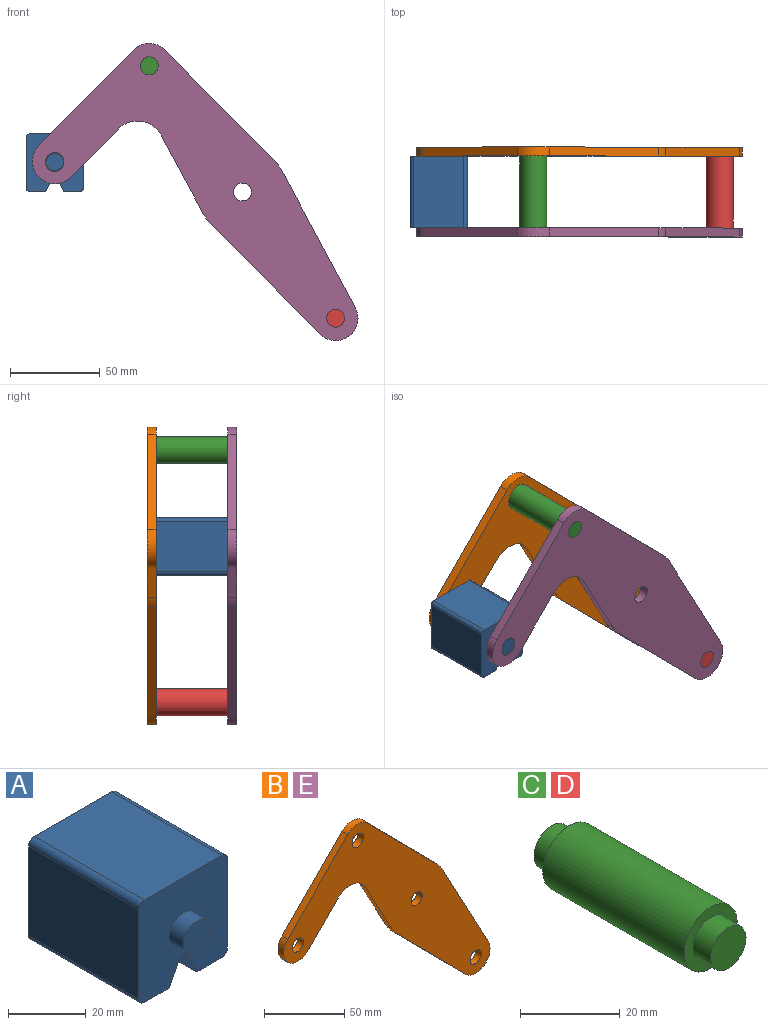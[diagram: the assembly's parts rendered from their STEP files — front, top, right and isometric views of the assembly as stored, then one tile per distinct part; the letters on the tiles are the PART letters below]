
ASSEMBLY  parts=5 mates=3
PART A: 18 faces, bbox 32.1x50x32.1 mm
  f0: plane 40x28.08mm, normal (1,0,0), area 1123.1mm2, adj f4,f10,f13,f14
  f1: plane 40x9.04mm, normal (0,0,-1), area 361.6mm2, adj f2,f4,f10,f14
  f2: plane 40x6.42mm, normal (-0.89,0,-0.45), area 287.2mm2, adj f1,f4,f10,f15
  f3: plane 40x6.42mm, normal (0.89,0,-0.45), area 287.2mm2, adj f4,f5,f10,f15
  f4: plane 32.08x32.08mm, normal (0,-1,0), area 900.6mm2, adj f0,f1,f2,f3,f5,f6,f7,f9
  f5: plane 40x9.04mm, normal (0,0,-1), area 361.6mm2, adj f3,f4,f10,f16
  f6: plane 40x28.08mm, normal (0,0,1), area 1123.1mm2, adj f4,f10,f13,f17
  f7: plane 40x28.08mm, normal (-1,0,0), area 1123.1mm2, adj f4,f10,f16,f17
  f8: plane 10x10mm, normal (0,-1,0), area 78.5mm2, adj f9
  f9: cylinder r=5mm len=10mm, axis (0,1,0), area 157.1mm2, adj f4,f8
  f10: plane 32.08x32.08mm, normal (0,1,0), area 900.6mm2, adj f0,f1,f2,f3,f5,f6,f7,f12
  f11: plane 10x10mm, normal (0,1,0), area 78.5mm2, adj f12
  f12: cylinder r=5mm len=10mm, axis (0,-1,0), area 157.1mm2, adj f10,f11
  f13: cylinder r=2mm len=40mm, axis (0,1,0), area 125.7mm2, adj f0,f4,f6,f10
  f14: cylinder r=2mm len=40mm, axis (0,-1,0), area 125.7mm2, adj f0,f1,f4,f10
  f15: cylinder r=2mm len=40mm, axis (0,1,0), area 177.1mm2, adj f2,f3,f4,f10
  f16: cylinder r=2mm len=40mm, axis (0,1,0), area 125.7mm2, adj f4,f5,f7,f10
  f17: cylinder r=2mm len=40mm, axis (0,-1,0), area 125.7mm2, adj f4,f6,f7,f10
PART B: 18 faces, bbox 181.7x5x165.8 mm
  f0: plane 43.49x23.35mm, normal (-0.88,0,-0.47), area 246.8mm2, adj f1,f14,f16,f17
  f1: cylinder r=25mm len=5.75mm, axis (0,1,0), area 35.8mm2, adj f0,f2,f16,f17
  f2: plane 61.6x60.87mm, normal (-0.71,0,-0.7), area 433mm2, adj f1,f3,f16,f17
  f3: cylinder r=12.5mm len=21.39mm, axis (0,1,0), area 178.4mm2, adj f2,f4,f16,f17
  f4: plane 76.3x40.96mm, normal (0.88,0,0.47), area 433mm2, adj f3,f5,f16,f17
  f5: cylinder r=25mm len=5.75mm, axis (0,1,0), area 35.8mm2, adj f4,f6,f16,f17
  f6: plane 61.6x60.87mm, normal (0.71,0,0.7), area 433mm2, adj f5,f7,f16,f17
  f7: cylinder r=12.5mm len=17.78mm, axis (0,1,0), area 98.9mm2, adj f6,f8,f16,f17
  f8: plane 53.35x52.71mm, normal (-0.71,0,0.7), area 375mm2, adj f7,f9,f16,f17
  f9: cylinder r=12.5mm len=21.39mm, axis (0,1,0), area 196.3mm2, adj f8,f10,f16,f17
  f10: plane 26.86x26.54mm, normal (0.71,0,-0.7), area 188.8mm2, adj f9,f14,f16,f17
  f11: cylinder r=5mm len=10mm, axis (0,1,0), area 157.1mm2, adj f16,f17
  f12: cylinder r=5mm len=10mm, axis (0,1,0), area 157.1mm2, adj f16,f17
  f13: cylinder r=5mm len=10mm, axis (0,1,0), area 157.1mm2, adj f16,f17
  f14: cylinder r=15mm len=23.89mm, axis (0,1,0), area 140.2mm2, adj f0,f10,f16,f17
  f15: cylinder r=5mm len=10mm, axis (0,1,0), area 157.1mm2, adj f16,f17
  f16: plane 181.66x165.78mm, normal (0,-1,0), area 8710.1mm2, adj f0,f1,f2,f3,f4,f5,f6,f7
  f17: plane 181.66x165.78mm, normal (0,1,0), area 8710.1mm2, adj f0,f1,f2,f3,f4,f5,f6,f7
PART C: 7 faces, bbox 15x50x15 mm
  f0: cylinder r=7.5mm len=40mm, axis (0,-1,0), area 1885mm2, adj f2,f5
  f1: cylinder r=5mm len=10mm, axis (0,1,0), area 157.1mm2, adj f2,f3
  f2: plane 15x15mm, normal (0,-1,0), area 98.2mm2, adj f0,f1
  f3: plane 10x10mm, normal (0,-1,0), area 78.5mm2, adj f1
  f4: cylinder r=5mm len=10mm, axis (0,-1,0), area 157.1mm2, adj f5,f6
  f5: plane 15x15mm, normal (0,1,0), area 98.2mm2, adj f0,f4
  f6: plane 10x10mm, normal (0,1,0), area 78.5mm2, adj f4
PART D: same geometry as C
PART E: same geometry as B
PLACE A t=(-56.86,-15.05,80.34)mm
PLACE B t=(-56.86,29.95,81.02)mm
PLACE C t=(-56.86,-15.05,81.02)mm
PLACE D t=(47.09,-15.05,-59.76)mm
PLACE E t=(-56.86,-15.05,81.02)mm fixed
MATE fastened E.f3 <-> D.f0  axis (0,1,0) through (-4.88,-15.05,10.63)mm
MATE fastened C.f0 <-> B.f7  axis (0,1,0) through (-108.84,24.95,151.41)mm
MATE revolute E.f9 <-> A.f4  axis (0,1,0) through (-161.55,-15.05,98.06)mm
